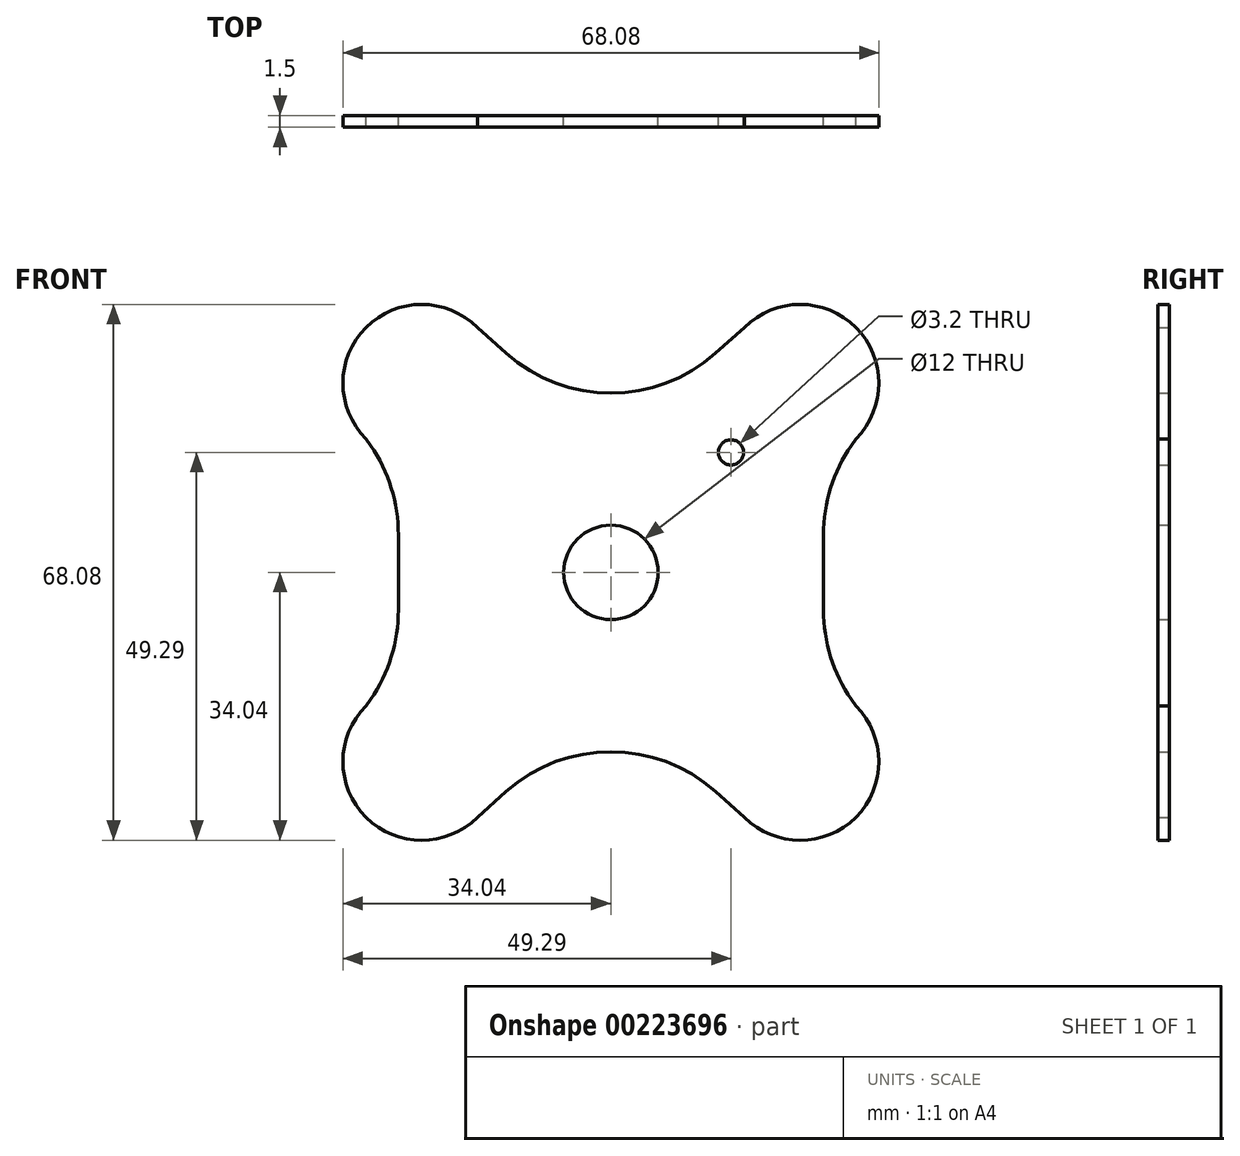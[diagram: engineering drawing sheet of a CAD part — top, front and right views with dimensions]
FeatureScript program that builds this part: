
annotation { "Feature Type Name" : "Feature", "Feature Type Description" : "" }
export const myFeature = defineFeature(function(context is Context, id is Id, definition is map)
    precondition{}
    {
        {
            var Q0;
            Q0=qCreatedBy(makeId("Front.planeOp"),FACE);
            var sketch = newSketch(context, id + "F0", { "sketchPlane" : qUnion([Q0])});
            skPoint(sketch, "E0", {"position": v(0, 0) * mm});
            skCircle(sketch, "E1", {"center": v(15.25, 15.25) * mm, "radius": 1.6 * mm});
            skLineSegment(sketch, "E2", {"start": v(-29.28, -29.28) * mm, "end": v(35.77, 35.77) * mm, "construction": true});
            skPoint(sketch, "E3", {"position": v(0, 16) * mm});
            skLineSegment(sketch, "E4", {"start": v(16.97, 31.11) * mm, "end": v(13.3, 27.84) * mm});
            skLineSegment(sketch, "E5", {"start": v(27, 4.78) * mm, "end": v(27, -4.78) * mm});
            skLineSegment(sketch, "E6", {"start": v(31.11, 16.97) * mm, "end": v(30.53, 16.12) * mm});
            skLineSegment(sketch, "E7.MirrorCS", {"start": v(-27, 4.78) * mm, "end": v(-27, -4.78) * mm});
            skLineSegment(sketch, "E8.MirrorCS", {"start": v(-31.11, 16.97) * mm, "end": v(-30.53, 16.12) * mm});
            skLineSegment(sketch, "E9.MirrorCS", {"start": v(-16.97, 31.11) * mm, "end": v(-13.3, 27.84) * mm});
            skArc(sketch, "E10.filletArc", {"start": v(-13.3, 27.84) * mm, "mid": v(0, 22.78) * mm, "end": v(13.3, 27.84) * mm});
            skPoint(sketch, "E11.visualSharp", {"position": v(27, 11) * mm});
            skArc(sketch, "E11.filletArc", {"start": v(30.53, 16.12) * mm, "mid": v(27.9, 10.72) * mm, "end": v(27, 4.78) * mm});
            skPoint(sketch, "E12.visualSharp", {"position": v(-27, 11) * mm});
            skArc(sketch, "E12.filletArc", {"start": v(-27, 4.78) * mm, "mid": v(-27.9, 10.72) * mm, "end": v(-30.53, 16.12) * mm});
            skArc(sketch, "E13.MirrorCS", {"start": v(30.53, -16.12) * mm, "mid": v(27.9, -10.72) * mm, "end": v(27, -4.78) * mm});
            skLineSegment(sketch, "E14.MirrorCS", {"start": v(31.11, -16.97) * mm, "end": v(30.53, -16.12) * mm});
            skLineSegment(sketch, "E15.MirrorCS", {"start": v(16.97, -31.11) * mm, "end": v(13.3, -27.84) * mm});
            skArc(sketch, "E16.MirrorCS", {"start": v(-13.3, -27.84) * mm, "mid": v(0, -22.78) * mm, "end": v(13.3, -27.84) * mm});
            skLineSegment(sketch, "E17.MirrorCS", {"start": v(-16.97, -31.11) * mm, "end": v(-13.3, -27.84) * mm});
            skLineSegment(sketch, "E18.MirrorCS", {"start": v(-31.11, -16.97) * mm, "end": v(-30.53, -16.12) * mm});
            skArc(sketch, "E19.MirrorCS", {"start": v(-27, -4.78) * mm, "mid": v(-27.9, -10.72) * mm, "end": v(-30.53, -16.12) * mm});
            skPoint(sketch, "E20.orphan", {"position": v(27, -11) * mm});
            skPoint(sketch, "E21.orphan", {"position": v(-27, -11) * mm});
            skCircle(sketch, "E22", {"center": v(0, 0) * mm, "radius": 6 * mm});
            skArc(sketch, "E23", {"start": v(31.11, 16.97) * mm, "mid": v(31.11, 31.11) * mm, "end": v(16.97, 31.11) * mm});
            skArc(sketch, "E24.MirrorCS", {"start": v(-31.11, 16.97) * mm, "mid": v(-31.11, 31.11) * mm, "end": v(-16.97, 31.11) * mm});
            skArc(sketch, "E25.MirrorCS", {"start": v(-31.11, -16.97) * mm, "mid": v(-31.11, -31.11) * mm, "end": v(-16.97, -31.11) * mm});
            skArc(sketch, "E26.MirrorCS", {"start": v(31.11, -16.97) * mm, "mid": v(31.11, -31.11) * mm, "end": v(16.97, -31.11) * mm});
            skSolve(sketch);
        }
        {
            var Q0;
            Q0=qSketchRegion(id+"F0",true);
            extrude(context, id + "F1", {"entities" : qUnion([Q0]), "depth" : 1.5 * mm});
        }
    });
